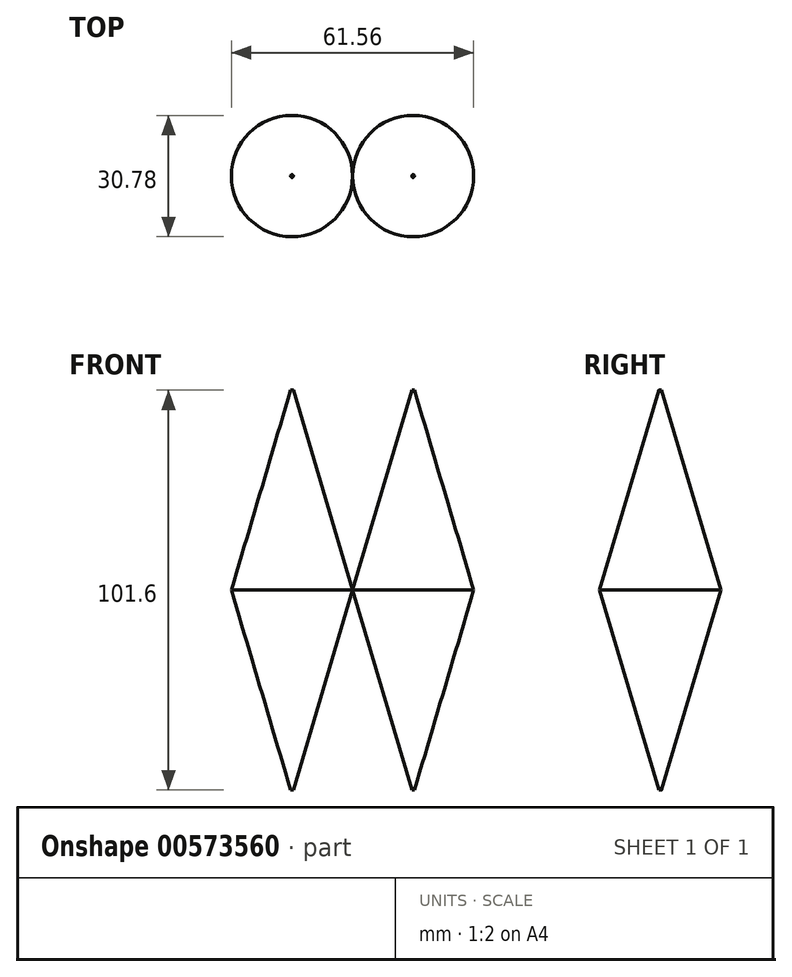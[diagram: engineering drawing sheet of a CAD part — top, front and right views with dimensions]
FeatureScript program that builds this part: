
annotation { "Feature Type Name" : "Feature", "Feature Type Description" : "" }
export const myFeature = defineFeature(function(context is Context, id is Id, definition is map)
    precondition{}
    {
        {
            var Q0;
            Q0=qCreatedBy(makeId("Top.planeOp"),FACE);
            var sketch = newSketch(context, id + "F0", { "sketchPlane" : qUnion([Q0])});
            skCircle(sketch, "E0", {"center": v(0, 0) * mm, "radius": 15.39 * mm});
            skSolve(sketch);
        }
        {
            var Q0;
            Q0 = qSketchRegion(id + "F0", true);
            extrude(context, id + "F1", {"entities" : qUnion([Q0]), "depth" : 50.8 * mm, "offsetDistance" : 25.4 * mm, "hasDraft" : true, "draftAngle" : 16.5 * degree, "draftPullDirection" : true});
        }
        {
            var Q0;
            Q0=makeQuery(id+"F1.opExtrude","SWEPT_BODY",BODY,{"disambiguationData":[OSD([sQuery(id+"F0.wireOp",EDGE,"E0")])]});
            var Q1;
            Q1=qCreatedBy(makeId("Top.planeOp"),FACE);
            mirror(context, id + "F2", {"operationType" : NewBodyOperationType.ADD, "entities" : qUnion([Q0]), "mirrorPlane" : qUnion([Q1])});
        }
        {
            var Q0;
            Q0=qCreatedBy(makeId("Right.planeOp"),FACE);
            cPlane(context, id + "F3", {"entities" : qUnion([Q0]), "cplaneType" : CPlaneType.OFFSET, "offset" : 15.4 * mm, "oppositeDirection" : true, "width" : 152.4 * mm, "height" : 152.4 * mm});
        }
        {
            var Q0;
            Q0=makeQuery(id+"F1.opExtrude","SWEPT_BODY",BODY,{"disambiguationData":[OSD([sQuery(id+"F0.wireOp",EDGE,"E0")])]});
            var Q1;
            Q1=qCreatedBy(id+"F3.planeOp",FACE);
            mirror(context, id + "F4", {"entities" : qUnion([Q0]), "mirrorPlane" : qUnion([Q1])});
        }
    });
